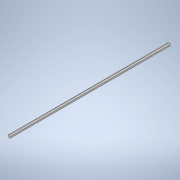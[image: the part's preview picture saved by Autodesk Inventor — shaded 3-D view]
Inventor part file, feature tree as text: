
AUTODESK INVENTOR PART (.ipt)
format: ipt  version: 2021 (Build 250183000, 183)  size: 125,440 bytes
history: native  units: in
note: dims shown in document units (in); Inventor stores cm internally (conversion verified against a paired STEP export)
features: sketch x2, extrude x1, other x1
ambient origin geometry x8: Origin, YZ Plane, XZ Plane, XY Plane, X Axis, Y Axis, Z Axis, Center Point
bodies: Solid2 (feature_tree), Solid1 (feature_tree)
feature tree (4):
  extrude  "Extrusion1"  [1 undecoded]
  sketch  "Sketch2"
  other  "Work Axis1"
  sketch  "Sketch1"  dims[d0=12.5in d1=0.0in]
note: 1 required parameter value undecoded (feature->parameter linkage not recoverable at this tier; creation-order binding heuristic only, values carry confidence <= 0.55)
